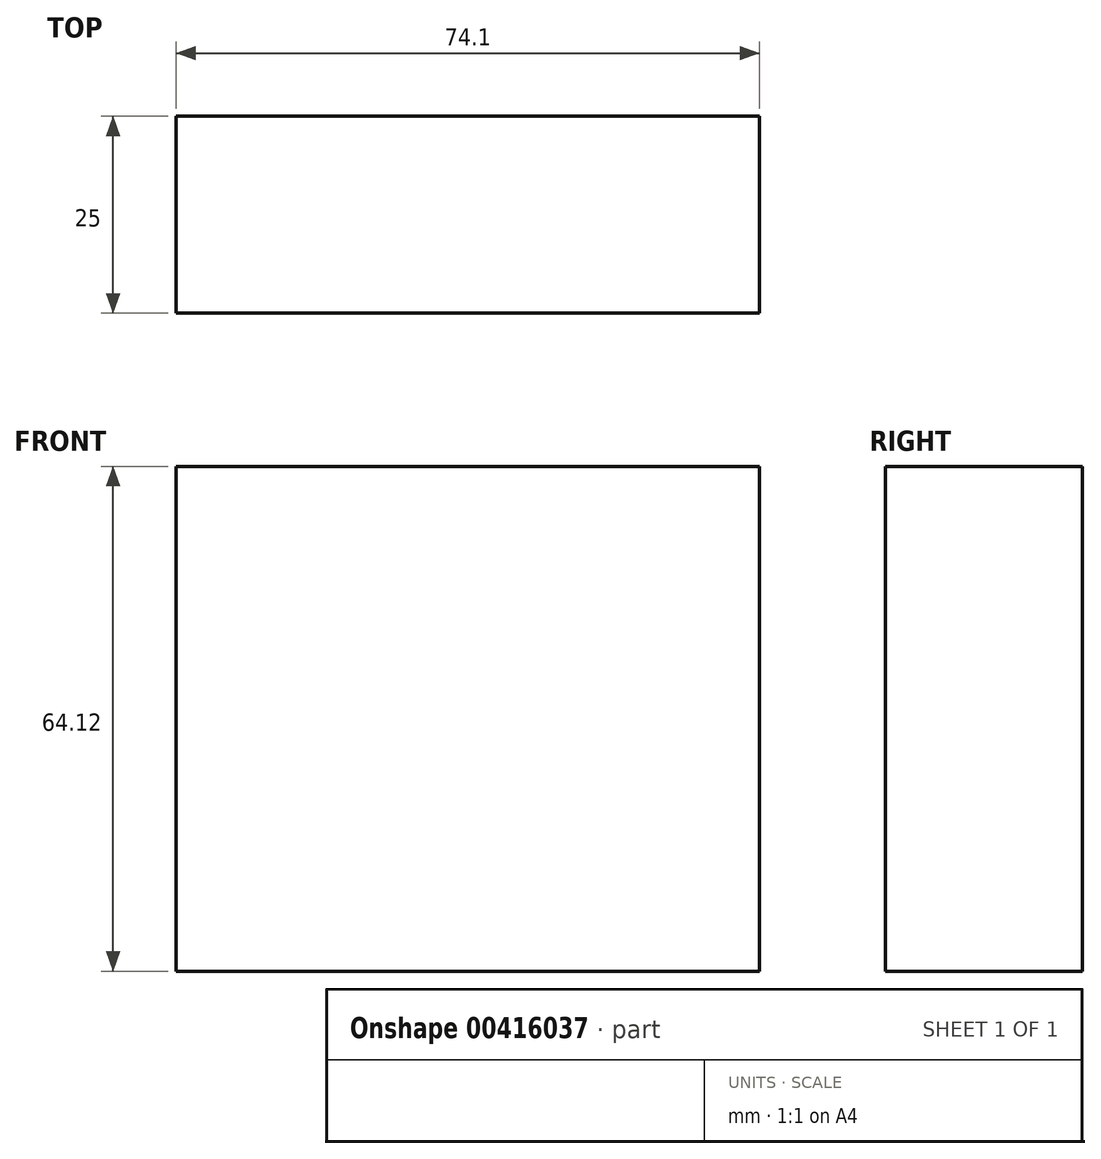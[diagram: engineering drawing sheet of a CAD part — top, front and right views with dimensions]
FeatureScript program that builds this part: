
annotation { "Feature Type Name" : "Feature", "Feature Type Description" : "" }
export const myFeature = defineFeature(function(context is Context, id is Id, definition is map)
    precondition{}
    {
        {
            var Q0;
            Q0=qCreatedBy(makeId("Front.planeOp"),FACE);
            var sketch = newSketch(context, id + "F0", { "sketchPlane" : qUnion([Q0])});
            skLineSegment(sketch, "E0.bottom", {"start": v(-105.48, 3.93) * mm, "end": v(-31.38, 3.93) * mm});
            skLineSegment(sketch, "E0.top", {"start": v(-105.48, 68.05) * mm, "end": v(-31.38, 68.05) * mm});
            skLineSegment(sketch, "E0.left", {"start": v(-105.48, 3.93) * mm, "end": v(-105.48, 68.05) * mm});
            skLineSegment(sketch, "E0.right", {"start": v(-31.38, 3.93) * mm, "end": v(-31.38, 68.05) * mm});
            skPoint(sketch, "E0.middle", {"position": v(-68.43, 35.99) * mm});
            skSolve(sketch);
        }
        {
            var Q0;
            Q0=makeQuery(id+"F0.imprint","IMPRINT",FACE,{"disambiguationData":[TD([[makeQuery(id+"F0.imprint","IMPRINT",EDGE,{"derivedFrom":sQuery(id+"F0.wireOp",EDGE,"E0.bottom")}),1.0]])]});
            extrude(context, id + "F1", {"entities" : qUnion([Q0]), "depth" : 25 * mm});
        }
    });
